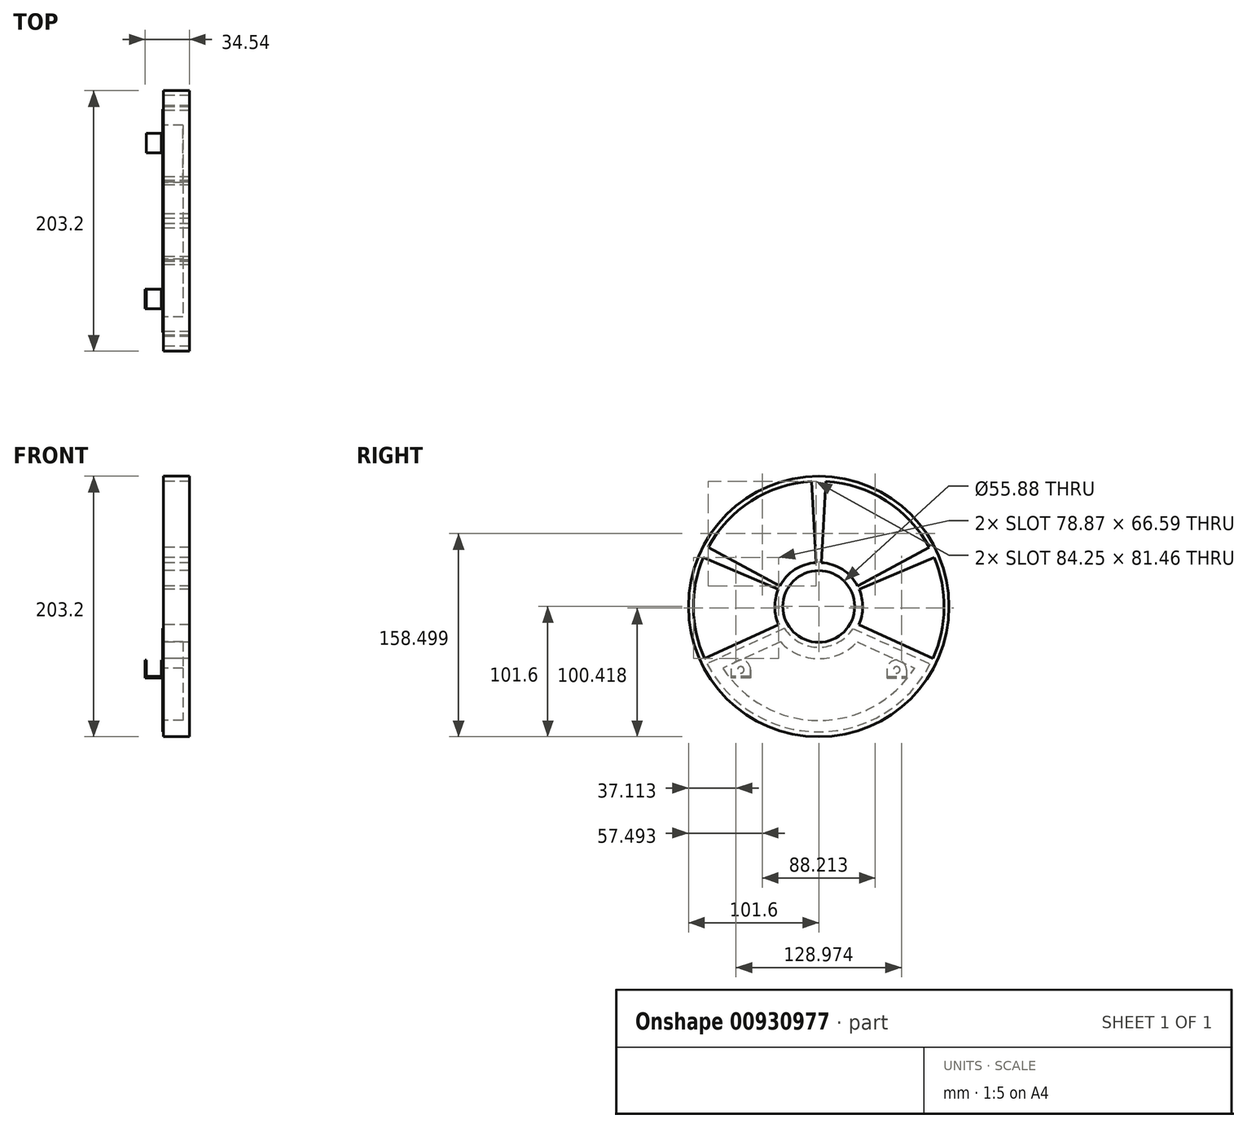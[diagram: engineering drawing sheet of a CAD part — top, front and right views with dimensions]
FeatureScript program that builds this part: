
annotation { "Feature Type Name" : "Feature", "Feature Type Description" : "" }
export const myFeature = defineFeature(function(context is Context, id is Id, definition is map)
    precondition{}
    {
        {
            var Q0;
            Q0=qCreatedBy(makeId("Right.planeOp"),FACE);
            var sketch = newSketch(context, id + "F0", { "sketchPlane" : qUnion([Q0])});
            skCircle(sketch, "E0", {"center": v(0, 0) * mm, "radius": 101.6 * mm});
            skCircle(sketch, "E1", {"center": v(0, 0) * mm, "radius": 27.94 * mm});
            skCircle(sketch, "E2", {"center": v(0, 0) * mm, "radius": 97.8 * mm});
            skLineSegment(sketch, "E3", {"start": v(0, 0) * mm, "end": v(0, 27.94) * mm, "construction": true});
            skLineSegment(sketch, "E4", {"start": v(-1.98, 34.23) * mm, "end": v(-5.65, 97.63) * mm});
            skLineSegment(sketch, "E5.MirrorCS", {"start": v(1.98, 34.23) * mm, "end": v(5.65, 97.63) * mm});
            skLineSegment(sketch, "E6", {"start": v(-30.24, 16.17) * mm, "end": v(-86.23, 46.12) * mm});
            skLineSegment(sketch, "E7", {"start": v(-31.56, 13.41) * mm, "end": v(-90, 38.25) * mm});
            skLineSegment(sketch, "E8.MirrorCS", {"start": v(30.24, 16.17) * mm, "end": v(86.23, 46.12) * mm});
            skLineSegment(sketch, "E9.MirrorCS", {"start": v(31.56, 13.41) * mm, "end": v(90, 38.25) * mm});
            skLineSegment(sketch, "E10", {"start": v(-31.2, -14.24) * mm, "end": v(-88.96, -40.62) * mm});
            skLineSegment(sketch, "E11.MirrorCS", {"start": v(31.2, -14.24) * mm, "end": v(88.96, -40.62) * mm});
            skCircle(sketch, "E12", {"center": v(0, 0) * mm, "radius": 34.3 * mm});
            skPoint(sketch, "E13.orphan", {"position": v(-25.42, -11.6) * mm});
            skLineSegment(sketch, "E14.trimOffspring", {"start": v(0, 34.3) * mm, "end": v(0, 97.8) * mm, "construction": true});
            skPoint(sketch, "E15.orphan", {"position": v(25.42, -11.6) * mm});
            skSolve(sketch);
        }
        {
            var Q0;
            Q0=makeQuery(id+"F0.imprint","IMPRINT",FACE,{"disambiguationData":[TD([[makeQuery(id+"F0.imprint","IMPRINT",EDGE,{"derivedFrom":sQuery(id+"F0.wireOp",EDGE,"E0")}),1.0]])]});
            var Q1;
            {var subQ0=sQuery(id+"F0.wireOp",EDGE,"E6");Q1=makeQuery(id+"F0.imprint","IMPRINT",FACE,{"disambiguationData":[TD([[makeQuery(id+"F0.imprint","IMPRINT",EDGE,{"derivedFrom":subQ0}),1.0]])]});}
            var Q2;
            Q2=makeQuery(id+"F0.imprint","IMPRINT",FACE,{"disambiguationData":[TD([[makeQuery(id+"F0.imprint","IMPRINT",EDGE,{"derivedFrom":sQuery(id+"F0.wireOp",EDGE,"E1")}),-1.0]])]});
            var Q3;
            {var subQ0=sQuery(id+"F0.wireOp",EDGE,"E8.MirrorCS");Q3=makeQuery(id+"F0.imprint","IMPRINT",FACE,{"disambiguationData":[TD([[makeQuery(id+"F0.imprint","IMPRINT",EDGE,{"derivedFrom":subQ0}),-1.0]])]});}
            var Q4;
            {var subQ0=sQuery(id+"F0.wireOp",EDGE,"E4");Q4=makeQuery(id+"F0.imprint","IMPRINT",FACE,{"disambiguationData":[TD([[makeQuery(id+"F0.imprint","IMPRINT",EDGE,{"derivedFrom":subQ0}),-1.0]])]});}
            var Q5;
            {var subQ0=sQuery(id+"F0.wireOp",EDGE,"E10");Q5=makeQuery(id+"F0.imprint","IMPRINT",FACE,{"disambiguationData":[TD([[makeQuery(id+"F0.imprint","IMPRINT",EDGE,{"derivedFrom":subQ0}),1.0]])]});}
            extrude(context, id + "F1", {"entities" : qUnion([Q0, Q1, Q2, Q3, Q4, Q5]), "depth" : 20.32 * mm, "offsetDistance" : 25.4 * mm});
        }
        {
            var Q0;
            Q0=makeQuery(id+"F1.opExtrude","CAP_FACE",FACE,{"disambiguationData":[OSD([sQuery(id+"F0.wireOp",EDGE,"E0"),sQuery(id+"F0.wireOp",EDGE,"E1"),sQuery(id+"F0.wireOp",EDGE,"E2"),sQuery(id+"F0.wireOp",EDGE,"E4"),sQuery(id+"F0.wireOp",EDGE,"E5.MirrorCS"),sQuery(id+"F0.wireOp",EDGE,"E6"),sQuery(id+"F0.wireOp",EDGE,"E7"),sQuery(id+"F0.wireOp",EDGE,"E8.MirrorCS"),sQuery(id+"F0.wireOp",EDGE,"E9.MirrorCS"),sQuery(id+"F0.wireOp",EDGE,"E10"),sQuery(id+"F0.wireOp",EDGE,"E11.MirrorCS"),sQuery(id+"F0.wireOp",EDGE,"E12")])],"isStart":true});
            var sketch = newSketch(context, id + "F2", { "sketchPlane" : qUnion([Q0])});
            skLineSegment(sketch, "E16.0", {"start": v(-29.84, -27.59) * mm, "end": v(-74.77, -48.1) * mm});
            skArc(sketch, "E17", {"start": v(-74.77, -48.1) * mm, "mid": v(0, -88.9) * mm, "end": v(74.77, -48.1) * mm});
            skArc(sketch, "E18", {"start": v(-29.84, -27.59) * mm, "mid": v(0, -40.64) * mm, "end": v(29.84, -27.59) * mm});
            skLineSegment(sketch, "E19.MirrorCS", {"start": v(29.84, -27.59) * mm, "end": v(74.77, -48.1) * mm});
            skPoint(sketch, "E20.orphan", {"position": v(-25.92, -25.8) * mm});
            skPoint(sketch, "E21.orphan", {"position": v(25.92, -25.8) * mm});
            skPoint(sketch, "E22.orphan", {"position": v(-83.68, -52.17) * mm});
            skPoint(sketch, "E23.orphan", {"position": v(83.68, -52.17) * mm});
            skSolve(sketch);
        }
        {
            var Q0;
            Q0=makeQuery(id+"F2.imprint","IMPRINT",FACE,{"disambiguationData":[TD([[makeQuery(id+"F2.imprint","IMPRINT",EDGE,{"derivedFrom":sQuery(id+"F2.wireOp",EDGE,"E16.0")}),1.0]])]});
            extrude(context, id + "F3", {"entities" : qUnion([Q0]), "operationType" : NewBodyOperationType.REMOVE, "oppositeDirection" : true, "depth" : 15.24 * mm, "offsetDistance" : 25.4 * mm});
        }
        {
            var Q0;
            Q0=qCreatedBy(makeId("Right.planeOp"),FACE);
            var sketch = newSketch(context, id + "F4", { "sketchPlane" : qUnion([Q0])});
            skArc(sketch, "E24", {"start": v(-26.75, -17.1) * mm, "mid": v(-0.06, -31.75) * mm, "end": v(26.7, -17.2) * mm});
            skArc(sketch, "E25", {"start": v(-87.02, -44.61) * mm, "mid": v(-0.06, -97.79) * mm, "end": v(86.97, -44.71) * mm});
            skLineSegment(sketch, "E26", {"start": v(-26.75, -17.1) * mm, "end": v(-87.02, -44.61) * mm});
            skLineSegment(sketch, "E27", {"start": v(26.7, -17.2) * mm, "end": v(86.97, -44.71) * mm});
            skSolve(sketch);
        }
        {
            var Q0;
            Q0=makeQuery(id+"F4.imprint","IMPRINT",FACE,{"disambiguationData":[TD([[makeQuery(id+"F4.imprint","IMPRINT",EDGE,{"derivedFrom":sQuery(id+"F4.wireOp",EDGE,"E24")}),-1.0]])]});
            extrude(context, id + "F5", {"entities" : qUnion([Q0]), "operationType" : NewBodyOperationType.ADD, "oppositeDirection" : true, "depth" : 0.76 * mm, "offsetDistance" : 25.4 * mm});
        }
        {
            var Q0;
            Q0=makeQuery(id+"F5.opExtrude","CAP_FACE",FACE,{"disambiguationData":[OSD([sQuery(id+"F4.wireOp",EDGE,"E24"),sQuery(id+"F4.wireOp",EDGE,"E25"),sQuery(id+"F4.wireOp",EDGE,"E26"),sQuery(id+"F4.wireOp",EDGE,"E27")])],"isStart":false});
            var sketch = newSketch(context, id + "F6", { "sketchPlane" : qUnion([Q0])});
            skArc(sketch, "E28", {"start": v(68.39, -49.39) * mm, "mid": v(60.77, -41.77) * mm, "end": v(53.15, -49.39) * mm});
            skLineSegment(sketch, "E29.top", {"start": v(53.15, -54.47) * mm, "end": v(68.39, -54.47) * mm});
            skLineSegment(sketch, "E29.left", {"start": v(53.15, -49.39) * mm, "end": v(53.15, -54.47) * mm});
            skLineSegment(sketch, "E29.right", {"start": v(68.39, -49.39) * mm, "end": v(68.39, -54.47) * mm});
            skLineSegment(sketch, "E30", {"start": v(0, 0) * mm, "end": v(0, -97.79) * mm, "construction": true});
            skPoint(sketch, "E30.endSnap0", {"position": v(0.06, -97.79) * mm});
            skLineSegment(sketch, "E31.MirrorCS", {"start": v(-53.15, -49.39) * mm, "end": v(-53.15, -54.47) * mm});
            skArc(sketch, "E32.MirrorCS", {"start": v(-68.39, -49.39) * mm, "mid": v(-60.77, -41.77) * mm, "end": v(-53.15, -49.39) * mm});
            skLineSegment(sketch, "E33.MirrorCS", {"start": v(-68.39, -49.39) * mm, "end": v(-68.39, -54.47) * mm});
            skLineSegment(sketch, "E34.MirrorCS", {"start": v(-53.15, -54.47) * mm, "end": v(-68.39, -54.47) * mm});
            skCircle(sketch, "E35", {"center": v(60.77, -49.39) * mm, "radius": 2.54 * mm});
            skCircle(sketch, "E36.MirrorC", {"center": v(-60.77, -49.39) * mm, "radius": 2.54 * mm});
            skLineSegment(sketch, "E37.top", {"start": v(53.15, -55.74) * mm, "end": v(68.39, -55.74) * mm});
            skLineSegment(sketch, "E37.left", {"start": v(53.15, -54.47) * mm, "end": v(53.15, -55.74) * mm});
            skLineSegment(sketch, "E37.right", {"start": v(68.39, -54.47) * mm, "end": v(68.39, -55.74) * mm});
            skLineSegment(sketch, "E38.MirrorCS", {"start": v(-53.15, -55.74) * mm, "end": v(-68.39, -55.74) * mm});
            skLineSegment(sketch, "E39.MirrorCS", {"start": v(-53.15, -54.47) * mm, "end": v(-53.15, -55.74) * mm});
            skLineSegment(sketch, "E40.MirrorCS", {"start": v(-68.39, -54.47) * mm, "end": v(-68.39, -55.74) * mm});
            skSolve(sketch);
        }
        {
            var Q0;
            Q0=makeQuery(id+"F6.imprint","IMPRINT",FACE,{"disambiguationData":[TD([[makeQuery(id+"F6.imprint","IMPRINT",EDGE,{"derivedFrom":sQuery(id+"F6.wireOp",EDGE,"E28")}),1.0]])]});
            var Q1;
            Q1=makeQuery(id+"F6.imprint","IMPRINT",FACE,{"disambiguationData":[TD([[makeQuery(id+"F6.imprint","IMPRINT",EDGE,{"derivedFrom":sQuery(id+"F6.wireOp",EDGE,"E31.MirrorCS")}),-1.0]])]});
            extrude(context, id + "F7", {"entities" : qUnion([Q0, Q1]), "operationType" : NewBodyOperationType.ADD, "depth" : 0.76 * mm, "offsetDistance" : 25.4 * mm});
        }
        {
            var Q0;
            Q0=makeQuery(id+"F6.imprint","IMPRINT",FACE,{"disambiguationData":[TD([[makeQuery(id+"F6.imprint","IMPRINT",EDGE,{"derivedFrom":sQuery(id+"F6.wireOp",EDGE,"E29.top")}),-1.0]])]});
            var Q1;
            Q1=makeQuery(id+"F6.imprint","IMPRINT",FACE,{"disambiguationData":[TD([[makeQuery(id+"F6.imprint","IMPRINT",EDGE,{"derivedFrom":sQuery(id+"F6.wireOp",EDGE,"E34.MirrorCS")}),1.0]])]});
            extrude(context, id + "F8", {"entities" : qUnion([Q0, Q1]), "operationType" : NewBodyOperationType.ADD, "depth" : 12.7 * mm, "offsetDistance" : 25.4 * mm});
        }
        {
            var Q0;
            Q0=makeQuery(id+"F8.opExtrude","CAP_FACE",FACE,{"disambiguationData":[OSD([sQuery(id+"F6.wireOp",EDGE,"E29.top"),sQuery(id+"F6.wireOp",EDGE,"E37.top"),sQuery(id+"F6.wireOp",EDGE,"E37.left"),sQuery(id+"F6.wireOp",EDGE,"E37.right")])],"isStart":false});
            var sketch = newSketch(context, id + "F9", { "sketchPlane" : qUnion([Q0])});
            skLineSegment(sketch, "E41.bottom", {"start": v(53.15, -55.74) * mm, "end": v(68.39, -55.74) * mm});
            skLineSegment(sketch, "E41.left", {"start": v(53.15, -55.74) * mm, "end": v(53.15, -49.39) * mm});
            skLineSegment(sketch, "E41.right", {"start": v(68.39, -55.74) * mm, "end": v(68.39, -49.39) * mm});
            skArc(sketch, "E42", {"start": v(68.39, -49.39) * mm, "mid": v(60.77, -41.77) * mm, "end": v(53.15, -49.39) * mm});
            skCircle(sketch, "E43", {"center": v(60.77, -49.39) * mm, "radius": 2.54 * mm});
            skArc(sketch, "E44.MirrorCS", {"start": v(-68.39, -49.39) * mm, "mid": v(-60.77, -41.77) * mm, "end": v(-53.15, -49.39) * mm});
            skLineSegment(sketch, "E45.MirrorCS", {"start": v(-53.15, -55.74) * mm, "end": v(-68.39, -55.74) * mm});
            skLineSegment(sketch, "E46.MirrorCS", {"start": v(-53.15, -55.74) * mm, "end": v(-53.15, -49.39) * mm});
            skLineSegment(sketch, "E47.MirrorCS", {"start": v(-68.39, -55.74) * mm, "end": v(-68.39, -49.39) * mm});
            skCircle(sketch, "E48.MirrorC", {"center": v(-60.77, -49.39) * mm, "radius": 2.54 * mm});
            skSolve(sketch);
        }
        {
            var Q0;
            Q0=makeQuery(id+"F9.imprint","IMPRINT",FACE,{"disambiguationData":[TD([[makeQuery(id+"F9.imprint","IMPRINT",EDGE,{"derivedFrom":sQuery(id+"F9.wireOp",EDGE,"E44.MirrorCS")}),-1.0]])]});
            var Q1;
            {var subQ0=sQuery(id+"F9.wireOp",EDGE,"E42");Q1=makeQuery(id+"F9.imprint","IMPRINT",FACE,{"disambiguationData":[TD([[makeQuery(id+"F9.imprint","IMPRINT",EDGE,{"derivedFrom":subQ0}),1.0]])]});}
            var Q2;
            {var subQ0=sQuery(id+"F9.wireOp",EDGE,"E41.bottom");Q2=makeQuery(id+"F9.imprint","IMPRINT",FACE,{"disambiguationData":[TD([[makeQuery(id+"F9.imprint","IMPRINT",EDGE,{"derivedFrom":subQ0}),1.0]])]});}
            extrude(context, id + "F10", {"entities" : qUnion([Q0, Q1, Q2]), "operationType" : NewBodyOperationType.ADD, "depth" : 0.76 * mm, "offsetDistance" : 25.4 * mm});
        }
    });
